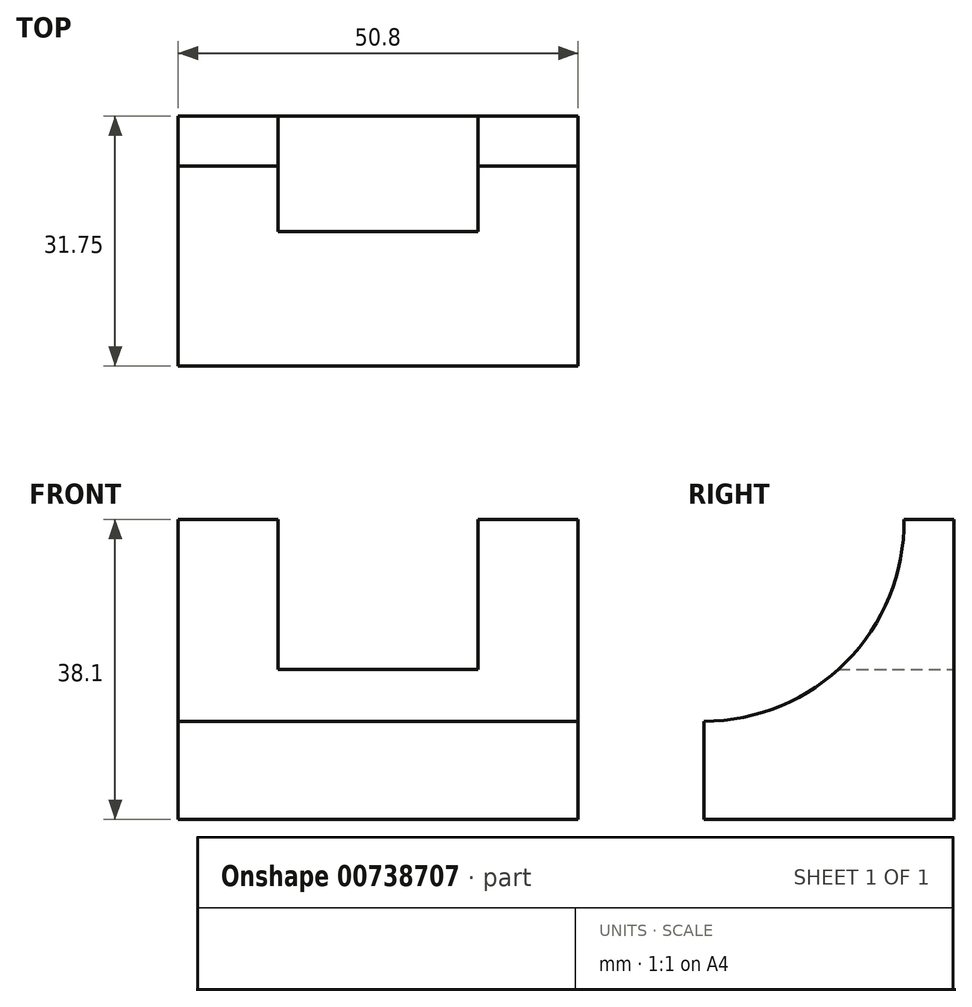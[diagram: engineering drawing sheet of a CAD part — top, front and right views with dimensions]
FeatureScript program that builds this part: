
annotation { "Feature Type Name" : "Feature", "Feature Type Description" : "" }
export const myFeature = defineFeature(function(context is Context, id is Id, definition is map)
    precondition{}
    {
        {
            var Q0;
            Q0=qCreatedBy(makeId("Front.planeOp"),FACE);
            var sketch = newSketch(context, id + "F0", { "sketchPlane" : qUnion([Q0])});
            skLineSegment(sketch, "E0", {"start": v(0, 38.1) * mm, "end": v(0, 0) * mm});
            skLineSegment(sketch, "E1", {"start": v(0, 0) * mm, "end": v(50.8, 0) * mm});
            skLineSegment(sketch, "E2", {"start": v(50.8, 0) * mm, "end": v(50.8, 38.1) * mm});
            skLineSegment(sketch, "E3", {"start": v(50.8, 38.1) * mm, "end": v(0, 38.1) * mm});
            skSolve(sketch);
        }
        {
            var Q0;
            Q0 = qSketchRegion(id + "F0", true);
            extrude(context, id + "F1", {"entities" : qUnion([Q0]), "depth" : 31.75 * mm, "offsetDistance" : 25.4 * mm});
        }
        {
            var Q0;
            Q0=qCreatedBy(makeId("Right.planeOp"),FACE);
            var sketch = newSketch(context, id + "F2", { "sketchPlane" : qUnion([Q0])});
            skCircle(sketch, "E4", {"center": v(-31.75, 37.88) * mm, "radius": 25.4 * mm});
            skSolve(sketch);
        }
        {
            var Q0;
            Q0 = qSketchRegion(id + "F2", true);
            extrude(context, id + "F3", {"entities" : qUnion([Q0]), "operationType" : NewBodyOperationType.REMOVE, "endBound" : BoundingType.THROUGH_ALL, "depth" : 25.4 * mm, "offsetDistance" : 25.4 * mm});
        }
        {
            var Q0;
            Q0=qCreatedBy(makeId("Front.planeOp"),FACE);
            var sketch = newSketch(context, id + "F4", { "sketchPlane" : qUnion([Q0])});
            skLineSegment(sketch, "E5", {"start": v(38.1, 38.1) * mm, "end": v(38.1, 19.05) * mm});
            skLineSegment(sketch, "E6", {"start": v(38.1, 19.05) * mm, "end": v(12.7, 19.05) * mm});
            skLineSegment(sketch, "E7", {"start": v(12.7, 19.05) * mm, "end": v(12.7, 38.1) * mm});
            skLineSegment(sketch, "E8", {"start": v(12.7, 38.1) * mm, "end": v(38.1, 38.1) * mm});
            skSolve(sketch);
        }
        {
            var Q0;
            Q0 = qSketchRegion(id + "F4", true);
            extrude(context, id + "F5", {"entities" : qUnion([Q0]), "operationType" : NewBodyOperationType.REMOVE, "endBound" : BoundingType.THROUGH_ALL, "depth" : 25.4 * mm, "offsetDistance" : 25.4 * mm});
        }
    });
